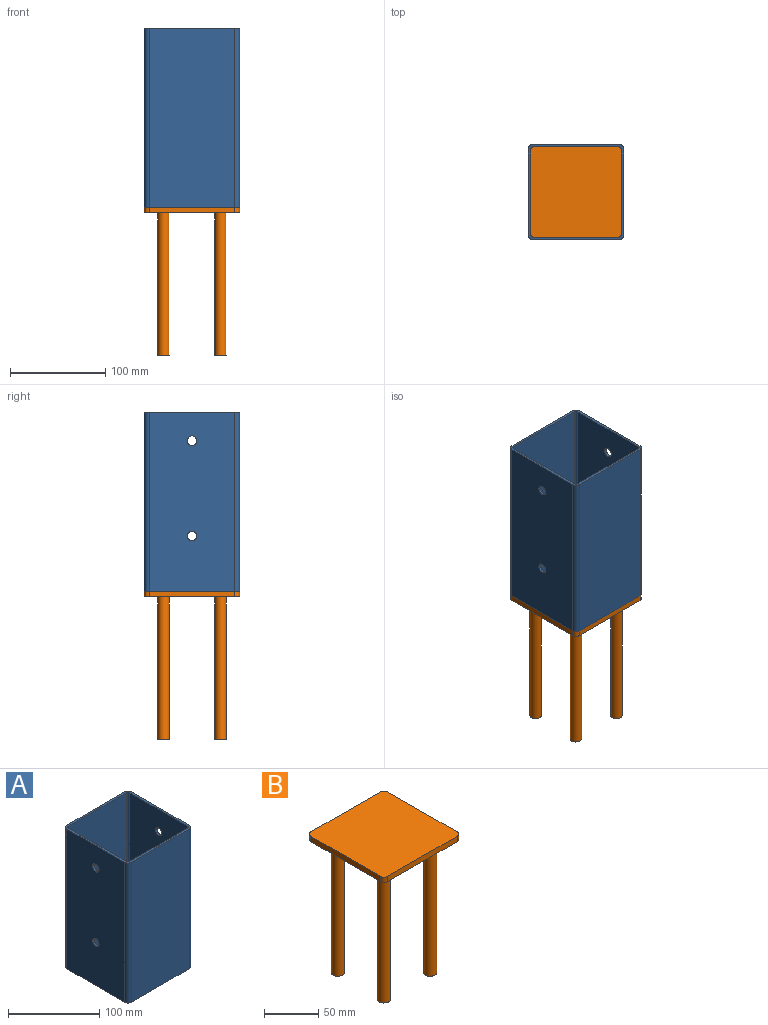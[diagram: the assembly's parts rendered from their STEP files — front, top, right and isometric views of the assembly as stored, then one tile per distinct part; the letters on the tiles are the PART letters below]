
ASSEMBLY  parts=2 mates=1
PART A: 22 faces, bbox 100x100x188 mm
  f0: plane 100x100mm, normal (0,0,1), area 958.9mm2, adj f2,f3,f4,f5,f6,f7,f8,f9
  f1: plane 100x100mm, normal (0,0,-1), area 958.9mm2, adj f2,f3,f4,f5,f6,f7,f8,f9
  f2: plane 188x90mm, normal (-1,0,0), area 16762.9mm2, adj f0,f1,f3,f9,f20,f21
  f3: cylinder r=5mm len=188mm, axis (0,0,-1), area 1476.5mm2, adj f0,f1,f2,f4
  f4: plane 188x90mm, normal (0,-1,0), area 16920mm2, adj f0,f1,f3,f5
  f5: cylinder r=5mm len=188mm, axis (0,0,-1), area 1476.5mm2, adj f0,f1,f4,f6
  f6: plane 188x90mm, normal (1,0,0), area 16762.9mm2, adj f0,f1,f5,f7,f18,f19
  f7: cylinder r=5mm len=188mm, axis (0,0,-1), area 1476.5mm2, adj f0,f1,f6,f8
  f8: plane 188x90mm, normal (0,1,0), area 16920mm2, adj f0,f1,f7,f9
  f9: cylinder r=5mm len=188mm, axis (0,0,-1), area 1476.5mm2, adj f0,f1,f2,f8
  f10: plane 188x90mm, normal (1,0,0), area 16762.9mm2, adj f0,f1,f11,f17,f20,f21
  f11: cylinder r=2.5mm len=188mm, axis (0,0,-1), area 738.3mm2, adj f0,f1,f10,f12
  f12: plane 188x90mm, normal (0,1,0), area 16920mm2, adj f0,f1,f11,f13
  f13: cylinder r=2.5mm len=188mm, axis (0,0,-1), area 738.3mm2, adj f0,f1,f12,f14
  f14: plane 188x90mm, normal (-1,0,0), area 16762.9mm2, adj f0,f1,f13,f15,f18,f19
  f15: cylinder r=2.5mm len=188mm, axis (0,0,-1), area 738.3mm2, adj f0,f1,f14,f16
  f16: plane 188x90mm, normal (0,-1,0), area 16920mm2, adj f0,f1,f15,f17
  f17: cylinder r=2.5mm len=188mm, axis (0,0,-1), area 738.3mm2, adj f0,f1,f10,f16
  f18: cylinder r=5mm len=10mm, axis (-1,0,0), area 78.5mm2, adj f6,f14
  f19: cylinder r=5mm len=10mm, axis (-1,0,0), area 78.5mm2, adj f6,f14
  f20: cylinder r=5mm len=10mm, axis (-1,0,0), area 78.5mm2, adj f2,f10
  f21: cylinder r=5mm len=10mm, axis (-1,0,0), area 78.5mm2, adj f2,f10
PART B: 18 faces, bbox 100x100x156 mm
  f0: cylinder r=5mm len=6mm, axis (0,0,1), area 47.1mm2, adj f1,f7,f8,f9
  f1: plane 90x6mm, normal (-1,0,0), area 540mm2, adj f0,f2,f8,f9
  f2: cylinder r=5mm len=6mm, axis (0,0,1), area 47.1mm2, adj f1,f3,f8,f9
  f3: plane 90x6mm, normal (0,1,0), area 540mm2, adj f2,f4,f8,f9
  f4: cylinder r=5mm len=6mm, axis (0,0,1), area 47.1mm2, adj f3,f5,f8,f9
  f5: plane 90x6mm, normal (1,0,0), area 540mm2, adj f4,f6,f8,f9
  f6: cylinder r=5mm len=6mm, axis (0,0,1), area 47.1mm2, adj f5,f7,f8,f9
  f7: plane 90x6mm, normal (0,-1,0), area 540mm2, adj f0,f6,f8,f9
  f8: plane 100x100mm, normal (0,0,-1), area 9526.2mm2, adj f0,f1,f2,f3,f4,f5,f6,f7
  f9: plane 100x100mm, normal (0,0,1), area 9978.5mm2, adj f0,f1,f2,f3,f4,f5,f6,f7
  f10: cylinder r=6mm len=150mm, axis (0,0,1), area 5654.9mm2, adj f8,f11
  f11: plane 12x12mm, normal (0,0,-1), area 113.1mm2, adj f10
  f12: cylinder r=6mm len=150mm, axis (0,0,1), area 5654.9mm2, adj f8,f13
  f13: plane 12x12mm, normal (0,0,-1), area 113.1mm2, adj f12
  f14: cylinder r=6mm len=150mm, axis (0,0,1), area 5654.9mm2, adj f8,f15
  f15: plane 12x12mm, normal (0,0,-1), area 113.1mm2, adj f14
  f16: cylinder r=6mm len=150mm, axis (0,0,1), area 5654.9mm2, adj f8,f17
  f17: plane 12x12mm, normal (0,0,-1), area 113.1mm2, adj f16
PLACE A t=(50,-50,0)mm
PLACE B t=(50,-50,0)mm
MATE fastened A.f1 <-> B.f9  axis (0,0,-1) through (0,0,0)mm
